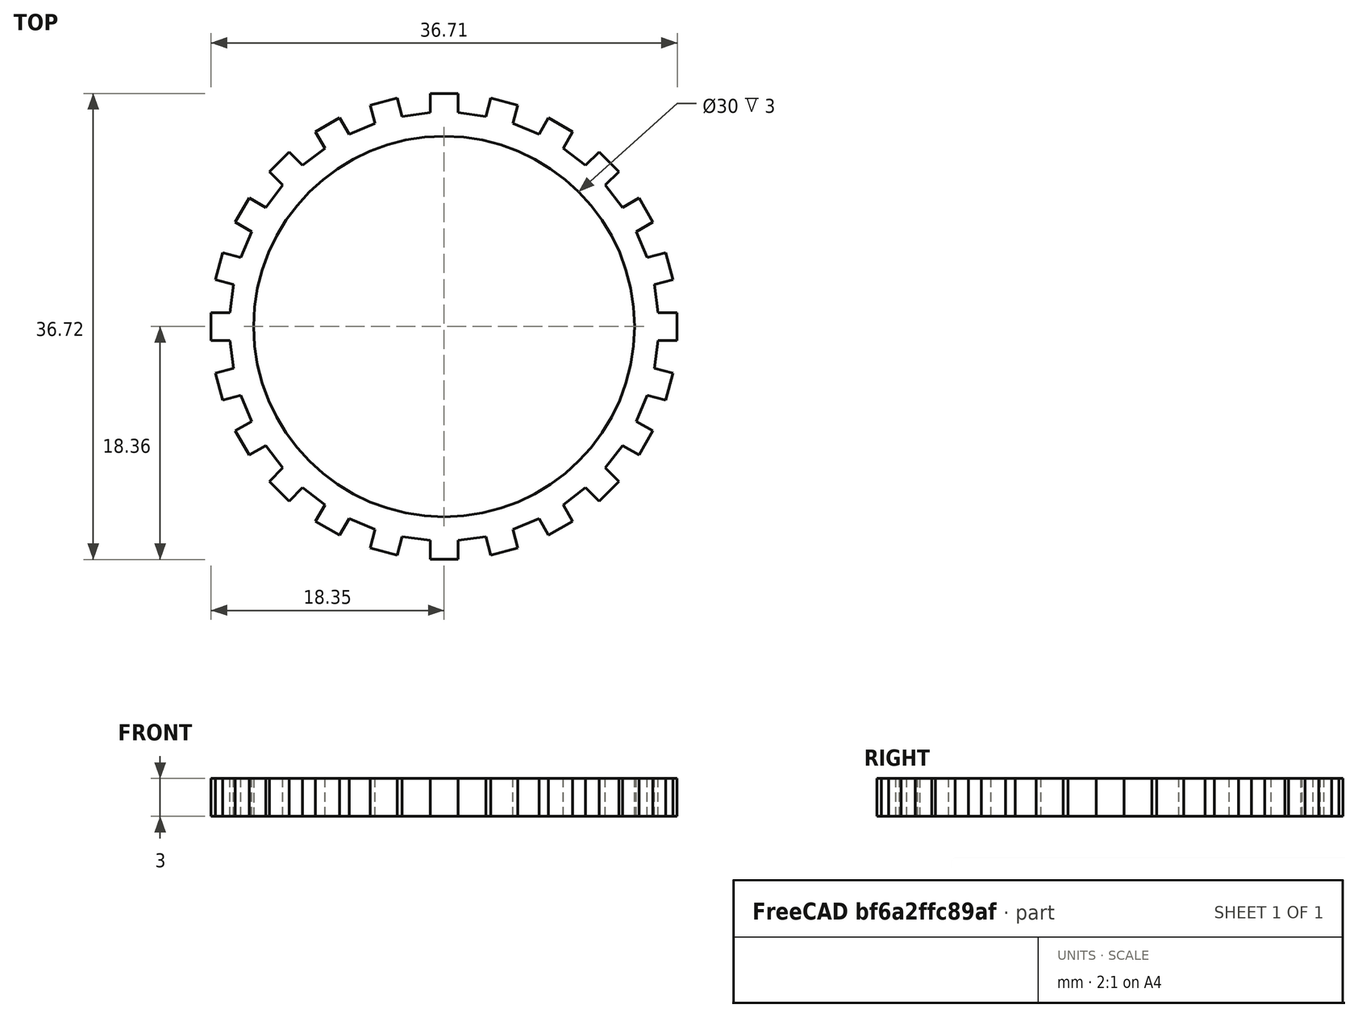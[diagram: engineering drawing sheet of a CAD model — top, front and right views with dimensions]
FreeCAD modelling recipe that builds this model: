
FCSTD DOCUMENT  (FreeCAD 0.19R24276 (Git))
Label: test_gear_1_0
License: All rights reserved
LicenseURL: http://en.wikipedia.org/wiki/All_rights_reserved
objects: Sketcher::SketchObject×1, PartDesign::Pad×1, PartDesign::Body×1
note: 4 computed .brp shape members not serialized (recipe doc carries the construction recipe); baked Part::Feature solids carry a one-line shape summary decoded from their .brp

FEATURE [Sketcher::SketchObject] Sketch
  FullyConstrained = false
  MapMode = 5
  Support = -> [XY_Plane]
  sketch-geometry (310):
    g0: Circle CenterX=0 CenterY=0 CenterZ=0 NormalX=0 NormalY=0 NormalZ=1 AngleXU=0 Radius=16.855
    g1: LineSegment StartX=0 StartY=16.855 StartZ=0 EndX=0 EndY=0 EndZ=0
    g2: LineSegment StartX=-4.3624 StartY=16.2807 StartZ=0 EndX=0 EndY=0 EndZ=0
    g3: LineSegment StartX=0 StartY=0 StartZ=0 EndX=4.3624 EndY=16.2807 EndZ=0
    g4: LineSegment StartX=0 StartY=0 StartZ=0 EndX=8.4275 EndY=14.5969 EndZ=0
    g5: LineSegment StartX=0 StartY=0 StartZ=0 EndX=11.9183 EndY=11.9183 EndZ=0
    g6: LineSegment StartX=0 StartY=0 StartZ=0 EndX=14.5969 EndY=8.4275 EndZ=0
    g7: LineSegment StartX=0 StartY=0 StartZ=0 EndX=16.2807 EndY=4.3624 EndZ=0
    g8: LineSegment StartX=0 StartY=0 StartZ=0 EndX=16.855 EndY=2.6e-15 EndZ=0
    g9: LineSegment StartX=-1.1 StartY=18.355 StartZ=0 EndX=-1.1 EndY=16.855 EndZ=0
    g10: LineSegment StartX=-1.1 StartY=16.855 StartZ=0 EndX=1.1 EndY=16.855 EndZ=0
    g11: LineSegment StartX=-1.1 StartY=18.355 StartZ=0 EndX=1.1 EndY=18.355 EndZ=0
    g12: GeomPoint X=0 Y=16.855 Z=0
    g13: LineSegment StartX=3.68811 StartY=18.0143 StartZ=0 EndX=3.29988 EndY=16.5654 EndZ=0
    g14: LineSegment StartX=3.29988 StartY=16.5654 StartZ=0 EndX=5.42491 EndY=15.996 EndZ=0
    g15: LineSegment StartX=3.68811 StartY=18.0143 StartZ=0 EndX=5.81314 EndY=17.4449 EndZ=0
    g16: LineSegment StartX=5.81314 StartY=17.4449 StartZ=0 EndX=5.42491 EndY=15.996 EndZ=0
    g17: GeomPoint X=4.3624 Y=16.2807 Z=0
    g18: LineSegment StartX=-10.1301 StartY=15.3459 StartZ=0 EndX=-9.38013 EndY=14.0469 EndZ=0
    g19: LineSegment StartX=-9.38013 StartY=14.0469 StartZ=0 EndX=-7.47487 EndY=15.1469 EndZ=0
    g20: LineSegment StartX=-10.1301 StartY=15.3459 StartZ=0 EndX=-8.22487 EndY=16.4459 EndZ=0
    g21: LineSegment StartX=-8.22487 StartY=16.4459 StartZ=0 EndX=-7.47487 EndY=15.1469 EndZ=0
    g22: GeomPoint X=-8.4275 Y=14.5969 Z=0
    g23: LineSegment StartX=0 StartY=0 StartZ=0 EndX=-8.4275 EndY=14.5969 EndZ=0
    g24: LineSegment StartX=-13.7568 StartY=12.2011 StartZ=0 EndX=-12.6961 EndY=11.1405 EndZ=0
    g25: LineSegment StartX=-12.6961 StartY=11.1405 StartZ=0 EndX=-11.1405 EndY=12.6961 EndZ=0
    g26: LineSegment StartX=-13.7568 StartY=12.2011 StartZ=0 EndX=-12.2011 EndY=13.7568 EndZ=0
    g27: LineSegment StartX=-12.2011 StartY=13.7568 StartZ=0 EndX=-11.1405 EndY=12.6961 EndZ=0
    g28: GeomPoint X=-11.9183 Y=11.9183 Z=0
    g29: LineSegment StartX=0 StartY=0 StartZ=0 EndX=-11.9183 EndY=11.9183 EndZ=0
    g30: LineSegment StartX=-5.81314 StartY=17.4449 StartZ=0 EndX=-5.42491 EndY=15.996 EndZ=0
    g31: LineSegment StartX=-5.42491 StartY=15.996 StartZ=0 EndX=-3.29988 EndY=16.5654 EndZ=0
    g32: LineSegment StartX=-5.81314 StartY=17.4449 StartZ=0 EndX=-3.68811 EndY=18.0143 EndZ=0
    g33: LineSegment StartX=-3.68811 StartY=18.0143 StartZ=0 EndX=-3.29988 EndY=16.5654 EndZ=0
    g34: GeomPoint X=-4.3624 Y=16.2807 Z=0
    g35: LineSegment StartX=8.22487 StartY=16.4459 StartZ=0 EndX=7.47487 EndY=15.1469 EndZ=0
    g36: LineSegment StartX=7.47487 StartY=15.1469 StartZ=0 EndX=9.38013 EndY=14.0469 EndZ=0
    g37: LineSegment StartX=8.22487 StartY=16.4459 StartZ=0 EndX=10.1301 EndY=15.3459 EndZ=0
    g38: LineSegment StartX=10.1301 StartY=15.3459 StartZ=0 EndX=9.38013 EndY=14.0469 EndZ=0
    g39: GeomPoint X=8.4275 Y=14.5969 Z=0
    g40: LineSegment StartX=12.2011 StartY=13.7568 StartZ=0 EndX=11.1405 EndY=12.6961 EndZ=0
    g41: LineSegment StartX=11.1405 StartY=12.6961 StartZ=0 EndX=12.6961 EndY=11.1405 EndZ=0
    g42: LineSegment StartX=12.2011 StartY=13.7568 StartZ=0 EndX=13.7568 EndY=12.2011 EndZ=0
    g43: LineSegment StartX=13.7568 StartY=12.2011 StartZ=0 EndX=12.6961 EndY=11.1405 EndZ=0
    g44: GeomPoint X=11.9183 Y=11.9183 Z=0
    g45: LineSegment StartX=15.3459 StartY=10.1301 StartZ=0 EndX=14.0469 EndY=9.38013 EndZ=0
    g46: LineSegment StartX=14.0469 StartY=9.38013 StartZ=0 EndX=15.1469 EndY=7.47487 EndZ=0
    g47: LineSegment StartX=15.3459 StartY=10.1301 StartZ=0 EndX=16.4459 EndY=8.22487 EndZ=0
    g48: LineSegment StartX=16.4459 StartY=8.22487 StartZ=0 EndX=15.1469 EndY=7.47487 EndZ=0
    g49: GeomPoint X=14.5969 Y=8.4275 Z=0
    g50: LineSegment StartX=17.4449 StartY=5.81314 StartZ=0 EndX=15.996 EndY=5.42491 EndZ=0
    g51: LineSegment StartX=15.996 StartY=5.42491 StartZ=0 EndX=16.5654 EndY=3.29988 EndZ=0
    g52: LineSegment StartX=17.4449 StartY=5.81314 StartZ=0 EndX=18.0143 EndY=3.68811 EndZ=0
    g53: LineSegment StartX=18.0143 StartY=3.68811 StartZ=0 EndX=16.5654 EndY=3.29988 EndZ=0
    g54: GeomPoint X=16.2807 Y=4.3624 Z=0
    g55: LineSegment StartX=0 StartY=0 StartZ=0 EndX=16.855 EndY=3.2e-15 EndZ=0
    g56: LineSegment StartX=18.355 StartY=1.1 StartZ=0 EndX=16.855 EndY=1.1 EndZ=0
    g57: LineSegment StartX=16.855 StartY=1.1 StartZ=0 EndX=16.855 EndY=-1.1 EndZ=0
    g58: LineSegment StartX=18.355 StartY=1.1 StartZ=0 EndX=18.355 EndY=-1.1 EndZ=0
    g59: LineSegment StartX=18.355 StartY=-1.1 StartZ=0 EndX=16.855 EndY=-1.1 EndZ=0
    g60: GeomPoint X=16.855 Y=3.2e-15 Z=0
    g61: LineSegment StartX=18.0143 StartY=-3.68811 StartZ=0 EndX=16.5654 EndY=-3.29988 EndZ=0
    g62: LineSegment StartX=16.5654 StartY=-3.29988 StartZ=0 EndX=15.996 EndY=-5.42491 EndZ=0
    g63: LineSegment StartX=18.0143 StartY=-3.68811 StartZ=0 EndX=17.4449 EndY=-5.81314 EndZ=0
    g64: LineSegment StartX=17.4449 StartY=-5.81314 StartZ=0 EndX=15.996 EndY=-5.42491 EndZ=0
    g65: GeomPoint X=16.2807 Y=-4.3624 Z=0
    g66: LineSegment StartX=0 StartY=0 StartZ=0 EndX=16.2807 EndY=-4.3624 EndZ=0
    g67: LineSegment StartX=16.4459 StartY=-8.22487 StartZ=0 EndX=15.1469 EndY=-7.47487 EndZ=0
    g68: LineSegment StartX=15.1469 StartY=-7.47487 StartZ=0 EndX=14.0469 EndY=-9.38013 EndZ=0
    g69: LineSegment StartX=16.4459 StartY=-8.22487 StartZ=0 EndX=15.3459 EndY=-10.1301 EndZ=0
    g70: LineSegment StartX=15.3459 StartY=-10.1301 StartZ=0 EndX=14.0469 EndY=-9.38013 EndZ=0
    g71: GeomPoint X=14.5969 Y=-8.4275 Z=0
    g72: LineSegment StartX=0 StartY=0 StartZ=0 EndX=14.5969 EndY=-8.4275 EndZ=0
    g73: LineSegment StartX=-16.4459 StartY=8.22487 StartZ=0 EndX=-15.1469 EndY=7.47487 EndZ=0
    g74: LineSegment StartX=-15.1469 StartY=7.47487 StartZ=0 EndX=-14.0469 EndY=9.38013 EndZ=0
    g75: LineSegment StartX=-16.4459 StartY=8.22487 StartZ=0 EndX=-15.3459 EndY=10.1301 EndZ=0
    g76: LineSegment StartX=-15.3459 StartY=10.1301 StartZ=0 EndX=-14.0469 EndY=9.38013 EndZ=0
    g77: GeomPoint X=-14.5969 Y=8.4275 Z=0
    g78: LineSegment StartX=0 StartY=0 StartZ=0 EndX=-14.5969 EndY=8.4275 EndZ=0
    g79: LineSegment StartX=-15.1469 StartY=7.47487 StartZ=0 EndX=-16.4459 EndY=8.22487 EndZ=0
    g80: LineSegment StartX=-16.4459 StartY=8.22487 StartZ=0 EndX=-15.3459 EndY=10.1301 EndZ=0
    g81: LineSegment StartX=-15.3459 StartY=10.1301 StartZ=0 EndX=-14.0469 EndY=9.38013 EndZ=0
    g82: LineSegment StartX=-12.6961 StartY=11.1405 StartZ=0 EndX=-14.0469 EndY=9.38013 EndZ=0
    g83: LineSegment StartX=-12.6961 StartY=11.1405 StartZ=0 EndX=-13.7568 EndY=12.2011 EndZ=0
    g84: LineSegment StartX=-13.7568 StartY=12.2011 StartZ=0 EndX=-12.2011 EndY=13.7568 EndZ=0
    g85: LineSegment StartX=-12.2011 StartY=13.7568 StartZ=0 EndX=-11.1405 EndY=12.6961 EndZ=0
    g86: LineSegment StartX=-11.1405 StartY=12.6961 StartZ=0 EndX=-9.38013 EndY=14.0469 EndZ=0
    g87: LineSegment StartX=-9.38013 StartY=14.0469 StartZ=0 EndX=-10.1301 EndY=15.3459 EndZ=0
    g88: LineSegment StartX=-10.1301 StartY=15.3459 StartZ=0 EndX=-8.22487 EndY=16.4459 EndZ=0
    g89: LineSegment StartX=-8.22487 StartY=16.4459 StartZ=0 EndX=-7.47487 EndY=15.1469 EndZ=0
    g90: LineSegment StartX=-7.47487 StartY=15.1469 StartZ=0 EndX=-5.42491 EndY=15.996 EndZ=0
    g91: LineSegment StartX=-5.42491 StartY=15.996 StartZ=0 EndX=-5.81314 EndY=17.4449 EndZ=0
    g92: LineSegment StartX=-5.81314 StartY=17.4449 StartZ=0 EndX=-3.68811 EndY=18.0143 EndZ=0
    g93: LineSegment StartX=-3.68811 StartY=18.0143 StartZ=0 EndX=-3.29988 EndY=16.5654 EndZ=0
    g94: LineSegment StartX=-3.29988 StartY=16.5654 StartZ=0 EndX=-1.1 EndY=16.855 EndZ=0
    g95: LineSegment StartX=-1.1 StartY=16.855 StartZ=0 EndX=-1.1 EndY=18.355 EndZ=0
    g96: LineSegment StartX=-1.1 StartY=18.355 StartZ=0 EndX=1.1 EndY=18.355 EndZ=0
    g97: LineSegment StartX=-18.0156 StartY=3.68811 StartZ=0 EndX=-16.5667 EndY=3.29988 EndZ=0
    g98: LineSegment StartX=-16.5667 StartY=3.29988 StartZ=0 EndX=-15.9973 EndY=5.42491 EndZ=0
    g99: LineSegment StartX=-18.0156 StartY=3.68811 StartZ=0 EndX=-17.4462 EndY=5.81314 EndZ=0
    g100: LineSegment StartX=-17.4462 StartY=5.81314 StartZ=0 EndX=-15.9973 EndY=5.42491 EndZ=0
    g101: GeomPoint X=-16.282 Y=4.3624 Z=0
    g102: LineSegment StartX=-0.00134425 StartY=1.8e-15 StartZ=0 EndX=-16.282 EndY=4.3624 EndZ=0
    g103: LineSegment StartX=-16.5667 StartY=3.29988 StartZ=0 EndX=-18.0156 EndY=3.68811 EndZ=0
    g104: LineSegment StartX=-18.0156 StartY=3.68811 StartZ=0 EndX=-17.4462 EndY=5.81314 EndZ=0
    g105: LineSegment StartX=-17.4462 StartY=5.81314 StartZ=0 EndX=-15.9973 EndY=5.42491 EndZ=0
    g106: LineSegment StartX=-18.3549 StartY=-1.1 StartZ=0 EndX=-16.8549 EndY=-1.1 EndZ=0
    g107: LineSegment StartX=-16.8549 StartY=-1.1 StartZ=0 EndX=-16.8549 EndY=1.1 EndZ=0
    g108: LineSegment StartX=-18.3549 StartY=-1.1 StartZ=0 EndX=-18.3549 EndY=1.1 EndZ=0
    g109: LineSegment StartX=-18.3549 StartY=1.1 StartZ=0 EndX=-16.8549 EndY=1.1 EndZ=0
    g110: GeomPoint X=-16.8549 Y=-6.7e-15 Z=0
    g111: LineSegment StartX=9.05985e-05 StartY=2.3e-15 StartZ=0 EndX=-16.8549 EndY=-6.7e-15 EndZ=0
    g112: LineSegment StartX=-18.3549 StartY=-1.1 StartZ=0 EndX=-18.3549 EndY=1.1 EndZ=0
    g113: LineSegment StartX=-18.3549 StartY=1.1 StartZ=0 EndX=-16.8549 EndY=1.1 EndZ=0
    g114: LineSegment StartX=-15.1469 StartY=7.47487 StartZ=0 EndX=-15.9973 EndY=5.42491 EndZ=0
    g115: LineSegment StartX=-16.5667 StartY=3.29988 StartZ=0 EndX=-16.8549 EndY=1.1 EndZ=0
    g116: LineSegment StartX=4.3624 StartY=16.2807 StartZ=0 EndX=0 EndY=0 EndZ=0
    g117: LineSegment StartX=1.1 StartY=18.355 StartZ=0 EndX=1.1 EndY=16.855 EndZ=0
    g118: GeomPoint X=0 Y=16.855 Z=0
    g119: LineSegment StartX=10.1301 StartY=15.3459 StartZ=0 EndX=9.38013 EndY=14.0469 EndZ=0
    g120: LineSegment StartX=9.38013 StartY=14.0469 StartZ=0 EndX=7.47487 EndY=15.1469 EndZ=0
    g121: LineSegment StartX=10.1301 StartY=15.3459 StartZ=0 EndX=8.22487 EndY=16.4459 EndZ=0
    g122: LineSegment StartX=8.22487 StartY=16.4459 StartZ=0 EndX=7.47487 EndY=15.1469 EndZ=0
    g123: GeomPoint X=8.4275 Y=14.5969 Z=0
    g124: LineSegment StartX=0 StartY=0 StartZ=0 EndX=8.4275 EndY=14.5969 EndZ=0
    g125: LineSegment StartX=13.7568 StartY=12.2011 StartZ=0 EndX=12.6961 EndY=11.1405 EndZ=0
    g126: LineSegment StartX=12.6961 StartY=11.1405 StartZ=0 EndX=11.1405 EndY=12.6961 EndZ=0
    g127: LineSegment StartX=13.7568 StartY=12.2011 StartZ=0 EndX=12.2011 EndY=13.7568 EndZ=0
    g128: LineSegment StartX=12.2011 StartY=13.7568 StartZ=0 EndX=11.1405 EndY=12.6961 EndZ=0
    g129: GeomPoint X=11.9183 Y=11.9183 Z=0
    g130: LineSegment StartX=0 StartY=0 StartZ=0 EndX=11.9183 EndY=11.9183 EndZ=0
    g131: LineSegment StartX=5.81314 StartY=17.4449 StartZ=0 EndX=5.42491 EndY=15.996 EndZ=0
    g132: LineSegment StartX=5.42491 StartY=15.996 StartZ=0 EndX=3.29988 EndY=16.5654 EndZ=0
    g133: LineSegment StartX=5.81314 StartY=17.4449 StartZ=0 EndX=3.68811 EndY=18.0143 EndZ=0
    g134: LineSegment StartX=3.68811 StartY=18.0143 StartZ=0 EndX=3.29988 EndY=16.5654 EndZ=0
    g135: GeomPoint X=4.3624 Y=16.2807 Z=0
    g136: LineSegment StartX=16.4459 StartY=8.22487 StartZ=0 EndX=15.1469 EndY=7.47487 EndZ=0
    g137: LineSegment StartX=15.1469 StartY=7.47487 StartZ=0 EndX=14.0469 EndY=9.38013 EndZ=0
    g138: LineSegment StartX=16.4459 StartY=8.22487 StartZ=0 EndX=15.3459 EndY=10.1301 EndZ=0
    g139: LineSegment StartX=15.3459 StartY=10.1301 StartZ=0 EndX=14.0469 EndY=9.38013 EndZ=0
    g140: GeomPoint X=14.5969 Y=8.4275 Z=0
    g141: LineSegment StartX=0 StartY=0 StartZ=0 EndX=14.5969 EndY=8.4275 EndZ=0
    g142: LineSegment StartX=15.1469 StartY=7.47487 StartZ=0 EndX=16.4459 EndY=8.22487 EndZ=0
    g143: LineSegment StartX=16.4459 StartY=8.22487 StartZ=0 EndX=15.3459 EndY=10.1301 EndZ=0
    g144: LineSegment StartX=15.3459 StartY=10.1301 StartZ=0 EndX=14.0469 EndY=9.38013 EndZ=0
    g145: LineSegment StartX=12.6961 StartY=11.1405 StartZ=0 EndX=14.0469 EndY=9.38013 EndZ=0
    g146: LineSegment StartX=12.6961 StartY=11.1405 StartZ=0 EndX=13.7568 EndY=12.2011 EndZ=0
    g147: LineSegment StartX=13.7568 StartY=12.2011 StartZ=0 EndX=12.2011 EndY=13.7568 EndZ=0
    g148: LineSegment StartX=12.2011 StartY=13.7568 StartZ=0 EndX=11.1405 EndY=12.6961 EndZ=0
    g149: LineSegment StartX=11.1405 StartY=12.6961 StartZ=0 EndX=9.38013 EndY=14.0469 EndZ=0
    g150: LineSegment StartX=9.38013 StartY=14.0469 StartZ=0 EndX=10.1301 EndY=15.3459 EndZ=0
    g151: LineSegment StartX=10.1301 StartY=15.3459 StartZ=0 EndX=8.22487 EndY=16.4459 EndZ=0
    g152: LineSegment StartX=8.22487 StartY=16.4459 StartZ=0 EndX=7.47487 EndY=15.1469 EndZ=0
    g153: LineSegment StartX=7.47487 StartY=15.1469 StartZ=0 EndX=5.42491 EndY=15.996 EndZ=0
    g154: LineSegment StartX=5.42491 StartY=15.996 StartZ=0 EndX=5.81314 EndY=17.4449 EndZ=0
    g155: LineSegment StartX=5.81314 StartY=17.4449 StartZ=0 EndX=3.68811 EndY=18.0143 EndZ=0
    g156: LineSegment StartX=3.68811 StartY=18.0143 StartZ=0 EndX=3.29988 EndY=16.5654 EndZ=0
    g157: LineSegment StartX=3.29988 StartY=16.5654 StartZ=0 EndX=1.1 EndY=16.855 EndZ=0
    g158: LineSegment StartX=18.0156 StartY=3.68811 StartZ=0 EndX=16.5667 EndY=3.29988 EndZ=0
    g159: LineSegment StartX=16.5667 StartY=3.29988 StartZ=0 EndX=15.9973 EndY=5.42491 EndZ=0
    g160: LineSegment StartX=18.0156 StartY=3.68811 StartZ=0 EndX=17.4462 EndY=5.81314 EndZ=0
    g161: LineSegment StartX=17.4462 StartY=5.81314 StartZ=0 EndX=15.9973 EndY=5.42491 EndZ=0
    g162: GeomPoint X=16.282 Y=4.3624 Z=0
    g163: LineSegment StartX=0.00134425 StartY=-1.2e-15 StartZ=0 EndX=16.282 EndY=4.3624 EndZ=0
    g164: LineSegment StartX=17.4462 StartY=5.81314 StartZ=0 EndX=15.9973 EndY=5.42491 EndZ=0
    g165: LineSegment StartX=18.3549 StartY=-1.1 StartZ=0 EndX=16.8549 EndY=-1.1 EndZ=0
    g166: LineSegment StartX=16.8549 StartY=-1.1 StartZ=0 EndX=16.8549 EndY=1.1 EndZ=0
    g167: LineSegment StartX=18.3549 StartY=-1.1 StartZ=0 EndX=18.3549 EndY=1.1 EndZ=0
    g168: LineSegment StartX=18.3549 StartY=1.1 StartZ=0 EndX=16.8549 EndY=1.1 EndZ=0
    g169: GeomPoint X=16.8549 Y=-7.1e-15 Z=0
    g170: LineSegment StartX=-9.05985e-05 StartY=1.7e-15 StartZ=0 EndX=16.8549 EndY=-7.1e-15 EndZ=0
    g171: LineSegment StartX=18.3549 StartY=1.1 StartZ=0 EndX=16.8549 EndY=1.1 EndZ=0
    g172: LineSegment StartX=15.1469 StartY=7.47487 StartZ=0 EndX=15.9973 EndY=5.42491 EndZ=0
    g173: LineSegment StartX=16.5667 StartY=3.29988 StartZ=0 EndX=16.8549 EndY=1.1 EndZ=0
    g174: LineSegment StartX=1.1 StartY=16.855 StartZ=0 EndX=1.1 EndY=18.355 EndZ=0
    g175: LineSegment StartX=-1.1 StartY=-18.355 StartZ=0 EndX=-1.1 EndY=-16.855 EndZ=0
    g176: LineSegment StartX=-1.1 StartY=-16.855 StartZ=0 EndX=1.1 EndY=-16.855 EndZ=0
    g177: LineSegment StartX=-1.1 StartY=-18.355 StartZ=0 EndX=1.1 EndY=-18.355 EndZ=0
    g178: GeomPoint X=1.08e-14 Y=-16.855 Z=0
    g179: LineSegment StartX=3.68811 StartY=-18.0143 StartZ=0 EndX=3.29988 EndY=-16.5654 EndZ=0
    g180: LineSegment StartX=3.29988 StartY=-16.5654 StartZ=0 EndX=5.42491 EndY=-15.996 EndZ=0
    g181: LineSegment StartX=3.68811 StartY=-18.0143 StartZ=0 EndX=5.81314 EndY=-17.4449 EndZ=0
    g182: LineSegment StartX=5.81314 StartY=-17.4449 StartZ=0 EndX=5.42491 EndY=-15.996 EndZ=0
    g183: GeomPoint X=4.3624 Y=-16.2807 Z=0
    g184: LineSegment StartX=-10.1301 StartY=-15.3459 StartZ=0 EndX=-9.38013 EndY=-14.0469 EndZ=0
    g185: LineSegment StartX=-9.38013 StartY=-14.0469 StartZ=0 EndX=-7.47487 EndY=-15.1469 EndZ=0
    g186: LineSegment StartX=-10.1301 StartY=-15.3459 StartZ=0 EndX=-8.22487 EndY=-16.4459 EndZ=0
    g187: LineSegment StartX=-8.22487 StartY=-16.4459 StartZ=0 EndX=-7.47487 EndY=-15.1469 EndZ=0
    g188: GeomPoint X=-8.4275 Y=-14.5969 Z=0
    g189: LineSegment StartX=-13.7568 StartY=-12.2011 StartZ=0 EndX=-12.6961 EndY=-11.1405 EndZ=0
    g190: LineSegment StartX=-12.6961 StartY=-11.1405 StartZ=0 EndX=-11.1405 EndY=-12.6961 EndZ=0
    g191: LineSegment StartX=-13.7568 StartY=-12.2011 StartZ=0 EndX=-12.2011 EndY=-13.7568 EndZ=0
    g192: LineSegment StartX=-12.2011 StartY=-13.7568 StartZ=0 EndX=-11.1405 EndY=-12.6961 EndZ=0
    g193: GeomPoint X=-11.9183 Y=-11.9183 Z=0
    g194: LineSegment StartX=-5.81314 StartY=-17.4449 StartZ=0 EndX=-5.42491 EndY=-15.996 EndZ=0
    g195: LineSegment StartX=-5.42491 StartY=-15.996 StartZ=0 EndX=-3.29988 EndY=-16.5654 EndZ=0
    g196: LineSegment StartX=-5.81314 StartY=-17.4449 StartZ=0 EndX=-3.68811 EndY=-18.0143 EndZ=0
    g197: LineSegment StartX=-3.68811 StartY=-18.0143 StartZ=0 EndX=-3.29988 EndY=-16.5654 EndZ=0
    g198: GeomPoint X=-4.3624 Y=-16.2807 Z=0
    g199: LineSegment StartX=8.22487 StartY=-16.4459 StartZ=0 EndX=7.47487 EndY=-15.1469 EndZ=0
    g200: LineSegment StartX=7.47487 StartY=-15.1469 StartZ=0 EndX=9.38013 EndY=-14.0469 EndZ=0
    g201: LineSegment StartX=8.22487 StartY=-16.4459 StartZ=0 EndX=10.1301 EndY=-15.3459 EndZ=0
    g202: LineSegment StartX=10.1301 StartY=-15.3459 StartZ=0 EndX=9.38013 EndY=-14.0469 EndZ=0
    g203: GeomPoint X=8.4275 Y=-14.5969 Z=0
    g204: LineSegment StartX=12.2011 StartY=-13.7568 StartZ=0 EndX=11.1405 EndY=-12.6961 EndZ=0
    g205: LineSegment StartX=11.1405 StartY=-12.6961 StartZ=0 EndX=12.6961 EndY=-11.1405 EndZ=0
    g206: LineSegment StartX=12.2011 StartY=-13.7568 StartZ=0 EndX=13.7568 EndY=-12.2011 EndZ=0
    g207: LineSegment StartX=13.7568 StartY=-12.2011 StartZ=0 EndX=12.6961 EndY=-11.1405 EndZ=0
    g208: GeomPoint X=11.9183 Y=-11.9183 Z=0
    g209: LineSegment StartX=15.3459 StartY=-10.1301 StartZ=0 EndX=14.0469 EndY=-9.38013 EndZ=0
    g210: LineSegment StartX=14.0469 StartY=-9.38013 StartZ=0 EndX=15.1469 EndY=-7.47487 EndZ=0
    g211: LineSegment StartX=15.3459 StartY=-10.1301 StartZ=0 EndX=16.4459 EndY=-8.22487 EndZ=0
    g212: LineSegment StartX=16.4459 StartY=-8.22487 StartZ=0 EndX=15.1469 EndY=-7.47487 EndZ=0
    g213: GeomPoint X=14.5969 Y=-8.4275 Z=0
    g214: LineSegment StartX=17.4449 StartY=-5.81314 StartZ=0 EndX=15.996 EndY=-5.42491 EndZ=0
    g215: LineSegment StartX=15.996 StartY=-5.42491 StartZ=0 EndX=16.5654 EndY=-3.29988 EndZ=0
    g216: LineSegment StartX=17.4449 StartY=-5.81314 StartZ=0 EndX=18.0143 EndY=-3.68811 EndZ=0
    g217: LineSegment StartX=18.0143 StartY=-3.68811 StartZ=0 EndX=16.5654 EndY=-3.29988 EndZ=0
    g218: GeomPoint X=16.2807 Y=-4.3624 Z=0
    g219: LineSegment StartX=18.355 StartY=-1.1 StartZ=0 EndX=16.855 EndY=-1.1 EndZ=0
    g220: LineSegment StartX=-16.4459 StartY=-8.22487 StartZ=0 EndX=-15.1469 EndY=-7.47487 EndZ=0
    g221: LineSegment StartX=-15.1469 StartY=-7.47487 StartZ=0 EndX=-14.0469 EndY=-9.38013 EndZ=0
    g222: LineSegment StartX=-16.4459 StartY=-8.22487 StartZ=0 EndX=-15.3459 EndY=-10.1301 EndZ=0
    g223: LineSegment StartX=-15.3459 StartY=-10.1301 StartZ=0 EndX=-14.0469 EndY=-9.38013 EndZ=0
    g224: GeomPoint X=-14.5969 Y=-8.4275 Z=0
    g225: LineSegment StartX=-15.1469 StartY=-7.47487 StartZ=0 EndX=-16.4459 EndY=-8.22487 EndZ=0
    g226: LineSegment StartX=-16.4459 StartY=-8.22487 StartZ=0 EndX=-15.3459 EndY=-10.1301 EndZ=0
    g227: LineSegment StartX=-15.3459 StartY=-10.1301 StartZ=0 EndX=-14.0469 EndY=-9.38013 EndZ=0
    g228: LineSegment StartX=-12.6961 StartY=-11.1405 StartZ=0 EndX=-14.0469 EndY=-9.38013 EndZ=0
    g229: LineSegment StartX=-12.6961 StartY=-11.1405 StartZ=0 EndX=-13.7568 EndY=-12.2011 EndZ=0
    g230: LineSegment StartX=-13.7568 StartY=-12.2011 StartZ=0 EndX=-12.2011 EndY=-13.7568 EndZ=0
    g231: LineSegment StartX=-12.2011 StartY=-13.7568 StartZ=0 EndX=-11.1405 EndY=-12.6961 EndZ=0
    g232: LineSegment StartX=-11.1405 StartY=-12.6961 StartZ=0 EndX=-9.38013 EndY=-14.0469 EndZ=0
    g233: LineSegment StartX=-9.38013 StartY=-14.0469 StartZ=0 EndX=-10.1301 EndY=-15.3459 EndZ=0
    g234: LineSegment StartX=-10.1301 StartY=-15.3459 StartZ=0 EndX=-8.22487 EndY=-16.4459 EndZ=0
    g235: LineSegment StartX=-8.22487 StartY=-16.4459 StartZ=0 EndX=-7.47487 EndY=-15.1469 EndZ=0
    g236: LineSegment StartX=-7.47487 StartY=-15.1469 StartZ=0 EndX=-5.42491 EndY=-15.996 EndZ=0
    g237: LineSegment StartX=-5.42491 StartY=-15.996 StartZ=0 EndX=-5.81314 EndY=-17.4449 EndZ=0
    g238: LineSegment StartX=-5.81314 StartY=-17.4449 StartZ=0 EndX=-3.68811 EndY=-18.0143 EndZ=0
    g239: LineSegment StartX=-3.68811 StartY=-18.0143 StartZ=0 EndX=-3.29988 EndY=-16.5654 EndZ=0
    g240: LineSegment StartX=-3.29988 StartY=-16.5654 StartZ=0 EndX=-1.1 EndY=-16.855 EndZ=0
    g241: LineSegment StartX=-1.1 StartY=-16.855 StartZ=0 EndX=-1.1 EndY=-18.355 EndZ=0
    g242: LineSegment StartX=-1.1 StartY=-18.355 StartZ=0 EndX=1.1 EndY=-18.355 EndZ=0
    g243: LineSegment StartX=-18.0156 StartY=-3.68811 StartZ=0 EndX=-16.5667 EndY=-3.29988 EndZ=0
    g244: LineSegment StartX=-16.5667 StartY=-3.29988 StartZ=0 EndX=-15.9973 EndY=-5.42491 EndZ=0
    g245: LineSegment StartX=-18.0156 StartY=-3.68811 StartZ=0 EndX=-17.4462 EndY=-5.81314 EndZ=0
    g246: LineSegment StartX=-17.4462 StartY=-5.81314 StartZ=0 EndX=-15.9973 EndY=-5.42491 EndZ=0
    g247: GeomPoint X=-16.282 Y=-4.3624 Z=0
    g248: LineSegment StartX=-16.5667 StartY=-3.29988 StartZ=0 EndX=-18.0156 EndY=-3.68811 EndZ=0
    g249: LineSegment StartX=-18.0156 StartY=-3.68811 StartZ=0 EndX=-17.4462 EndY=-5.81314 EndZ=0
    g250: LineSegment StartX=-17.4462 StartY=-5.81314 StartZ=0 EndX=-15.9973 EndY=-5.42491 EndZ=0
    g251: LineSegment StartX=-18.3549 StartY=-1.1 StartZ=0 EndX=-16.8549 EndY=-1.1 EndZ=0
    g252: LineSegment StartX=-18.3549 StartY=-1.1 StartZ=0 EndX=-16.8549 EndY=-1.1 EndZ=0
    g253: LineSegment StartX=-15.1469 StartY=-7.47487 StartZ=0 EndX=-15.9973 EndY=-5.42491 EndZ=0
    g254: LineSegment StartX=-16.5667 StartY=-3.29988 StartZ=0 EndX=-16.8549 EndY=-1.1 EndZ=0
    g255: LineSegment StartX=1.1 StartY=-18.355 StartZ=0 EndX=1.1 EndY=-16.855 EndZ=0
    g256: GeomPoint X=1.08e-14 Y=-16.855 Z=0
    g257: LineSegment StartX=10.1301 StartY=-15.3459 StartZ=0 EndX=9.38013 EndY=-14.0469 EndZ=0
    g258: LineSegment StartX=9.38013 StartY=-14.0469 StartZ=0 EndX=7.47487 EndY=-15.1469 EndZ=0
    g259: LineSegment StartX=10.1301 StartY=-15.3459 StartZ=0 EndX=8.22487 EndY=-16.4459 EndZ=0
    g260: LineSegment StartX=8.22487 StartY=-16.4459 StartZ=0 EndX=7.47487 EndY=-15.1469 EndZ=0
    g261: GeomPoint X=8.4275 Y=-14.5969 Z=0
    g262: LineSegment StartX=13.7568 StartY=-12.2011 StartZ=0 EndX=12.6961 EndY=-11.1405 EndZ=0
    g263: LineSegment StartX=12.6961 StartY=-11.1405 StartZ=0 EndX=11.1405 EndY=-12.6961 EndZ=0
    g264: LineSegment StartX=13.7568 StartY=-12.2011 StartZ=0 EndX=12.2011 EndY=-13.7568 EndZ=0
    g265: LineSegment StartX=12.2011 StartY=-13.7568 StartZ=0 EndX=11.1405 EndY=-12.6961 EndZ=0
    g266: GeomPoint X=11.9183 Y=-11.9183 Z=0
    g267: LineSegment StartX=5.81314 StartY=-17.4449 StartZ=0 EndX=5.42491 EndY=-15.996 EndZ=0
    g268: LineSegment StartX=5.42491 StartY=-15.996 StartZ=0 EndX=3.29988 EndY=-16.5654 EndZ=0
    g269: LineSegment StartX=5.81314 StartY=-17.4449 StartZ=0 EndX=3.68811 EndY=-18.0143 EndZ=0
    g270: LineSegment StartX=3.68811 StartY=-18.0143 StartZ=0 EndX=3.29988 EndY=-16.5654 EndZ=0
    g271: GeomPoint X=4.3624 Y=-16.2807 Z=0
    g272: LineSegment StartX=16.4459 StartY=-8.22487 StartZ=0 EndX=15.1469 EndY=-7.47487 EndZ=0
    g273: LineSegment StartX=15.1469 StartY=-7.47487 StartZ=0 EndX=14.0469 EndY=-9.38013 EndZ=0
    g274: LineSegment StartX=16.4459 StartY=-8.22487 StartZ=0 EndX=15.3459 EndY=-10.1301 EndZ=0
    g275: LineSegment StartX=15.3459 StartY=-10.1301 StartZ=0 EndX=14.0469 EndY=-9.38013 EndZ=0
    g276: GeomPoint X=14.5969 Y=-8.4275 Z=0
    g277: LineSegment StartX=15.1469 StartY=-7.47487 StartZ=0 EndX=16.4459 EndY=-8.22487 EndZ=0
    g278: LineSegment StartX=16.4459 StartY=-8.22487 StartZ=0 EndX=15.3459 EndY=-10.1301 EndZ=0
    g279: LineSegment StartX=15.3459 StartY=-10.1301 StartZ=0 EndX=14.0469 EndY=-9.38013 EndZ=0
    g280: LineSegment StartX=12.6961 StartY=-11.1405 StartZ=0 EndX=14.0469 EndY=-9.38013 EndZ=0
    g281: LineSegment StartX=12.6961 StartY=-11.1405 StartZ=0 EndX=13.7568 EndY=-12.2011 EndZ=0
    g282: LineSegment StartX=13.7568 StartY=-12.2011 StartZ=0 EndX=12.2011 EndY=-13.7568 EndZ=0
    g283: LineSegment StartX=12.2011 StartY=-13.7568 StartZ=0 EndX=11.1405 EndY=-12.6961 EndZ=0
    g284: LineSegment StartX=11.1405 StartY=-12.6961 StartZ=0 EndX=9.38013 EndY=-14.0469 EndZ=0
    g285: LineSegment StartX=9.38013 StartY=-14.0469 StartZ=0 EndX=10.1301 EndY=-15.3459 EndZ=0
    g286: LineSegment StartX=10.1301 StartY=-15.3459 StartZ=0 EndX=8.22487 EndY=-16.4459 EndZ=0
    g287: LineSegment StartX=8.22487 StartY=-16.4459 StartZ=0 EndX=7.47487 EndY=-15.1469 EndZ=0
    g288: LineSegment StartX=7.47487 StartY=-15.1469 StartZ=0 EndX=5.42491 EndY=-15.996 EndZ=0
    g289: LineSegment StartX=5.42491 StartY=-15.996 StartZ=0 EndX=5.81314 EndY=-17.4449 EndZ=0
    g290: LineSegment StartX=5.81314 StartY=-17.4449 StartZ=0 EndX=3.68811 EndY=-18.0143 EndZ=0
    g291: LineSegment StartX=3.68811 StartY=-18.0143 StartZ=0 EndX=3.29988 EndY=-16.5654 EndZ=0
    g292: LineSegment StartX=3.29988 StartY=-16.5654 StartZ=0 EndX=1.1 EndY=-16.855 EndZ=0
    g293: LineSegment StartX=18.0156 StartY=-3.68811 StartZ=0 EndX=16.5667 EndY=-3.29988 EndZ=0
    g294: LineSegment StartX=16.5667 StartY=-3.29988 StartZ=0 EndX=15.9973 EndY=-5.42491 EndZ=0
    g295: LineSegment StartX=18.0156 StartY=-3.68811 StartZ=0 EndX=17.4462 EndY=-5.81314 EndZ=0
    g296: LineSegment StartX=17.4462 StartY=-5.81314 StartZ=0 EndX=15.9973 EndY=-5.42491 EndZ=0
    g297: GeomPoint X=16.282 Y=-4.3624 Z=0
    g298: LineSegment StartX=16.5667 StartY=-3.29988 StartZ=0 EndX=18.0156 EndY=-3.68811 EndZ=0
    g299: LineSegment StartX=18.0156 StartY=-3.68811 StartZ=0 EndX=17.4462 EndY=-5.81314 EndZ=0
    g300: LineSegment StartX=17.4462 StartY=-5.81314 StartZ=0 EndX=15.9973 EndY=-5.42491 EndZ=0
    g301: LineSegment StartX=18.3549 StartY=-1.1 StartZ=0 EndX=16.8549 EndY=-1.1 EndZ=0
    g302: LineSegment StartX=15.1469 StartY=-7.47487 StartZ=0 EndX=15.9973 EndY=-5.42491 EndZ=0
    g303: LineSegment StartX=16.5667 StartY=-3.29988 StartZ=0 EndX=16.8549 EndY=-1.1 EndZ=0
    g304: LineSegment StartX=1.1 StartY=-16.855 StartZ=0 EndX=1.1 EndY=-18.355 EndZ=0
    g305: Circle CenterX=0 CenterY=0 CenterZ=0 NormalX=0 NormalY=0 NormalZ=1 AngleXU=0 Radius=15
    g306: LineSegment StartX=18.0156 StartY=3.68811 StartZ=0 EndX=16.5667 EndY=3.29988 EndZ=0
    g307: LineSegment StartX=17.4462 StartY=5.81314 StartZ=0 EndX=18.0156 EndY=3.68811 EndZ=0
    g308: LineSegment StartX=18.3549 StartY=1.1 StartZ=0 EndX=18.355 EndY=-1.1 EndZ=0
    g309: LineSegment StartX=18.355 StartY=-1.1 StartZ=0 EndX=16.8549 EndY=-1.1 EndZ=0
  constraints (689):
    c: Diameter(g0) = 33.71
    c: Vertical(g1)
    c: Coincident(g0,g-1)
    c: Coincident(g1,g0)
    c: Coincident(g2,g0)
    c: Angle(g1,g2) = 0.261799
    c: Coincident(g3,g0)
    c: Angle(g3,g1) = 0.261799
    c: PointOnObject(g3,g0)
    c: PointOnObject(g1,g0)
    c: PointOnObject(g2,g0)
    c: Coincident(g4,g0)
    c: Angle(g4,g3) = 0.261799
    c: PointOnObject(g4,g0)
    c: Coincident(g5,g0)
    c: Angle(g5,g4) = 0.261799
    c: Coincident(g6,g0)
    c: Angle(g6,g5) = 0.261799
    c: Coincident(g7,g0)
    c: Angle(g7,g6) = 0.261799
    c: Coincident(g8,g0)
    c: Angle(g8,g7) = 0.261799
    c: PointOnObject(g5,g0)
    c: PointOnObject(g7,g0)
    c: PointOnObject(g6,g0)
    c: PointOnObject(g8,g0)
    c: Coincident(g10,g9)
    c: Coincident(g11,g9)
    c: Parallel(g10,g11)
    c: Perpendicular(g10,g9)
    c: Distance(g9,g11) = 2.2
    c: Distance(g11,g10) = 1.5
    c: PointOnObject(g12,g10)
    c: Distance(g9,g12) = 1.1
    c: Coincident(g12,g1)
    c: Perpendicular(g1,g10)
    c: Coincident(g14,g13)
    c: Coincident(g15,g13)
    c: Coincident(g16,g15)
    c: Coincident(g16,g14)
    c: Parallel(g14,g15)
    c: Parallel(g13,g16)
    c: Perpendicular(g14,g13)
    c: Distance(g13,g15) = 2.2
    c: Distance(g15,g14) = 1.5
    c: PointOnObject(g17,g14)
    c: Distance(g13,g17) = 1.1
    c: Coincident(g17,g3)
    c: Perpendicular(g3,g14)
    c: Coincident(g19,g18)
    c: Coincident(g20,g18)
    c: Coincident(g21,g20)
    c: Coincident(g21,g19)
    c: Parallel(g19,g20)
    c: Parallel(g18,g21)
    c: Perpendicular(g19,g18)
    c: Distance(g18,g20) = 2.2
    c: Distance(g20,g19) = 1.5
    c: PointOnObject(g22,g19)
    c: Distance(g18,g22) = 1.1
    c: Perpendicular(g23,g19)
    c: Coincident(g23,g0)
    c: Angle(g23,g2) = -0.261799
    c: PointOnObject(g23,g0)
    c: Coincident(g22,g23)
    c: Coincident(g25,g24)
    c: Coincident(g26,g24)
    c: Coincident(g27,g26)
    c: Coincident(g27,g25)
    c: Parallel(g25,g26)
    c: Parallel(g24,g27)
    c: Perpendicular(g25,g24)
    c: Distance(g24,g26) = 2.2
    c: Distance(g26,g25) = 1.5
    c: PointOnObject(g28,g25)
    c: Distance(g24,g28) = 1.1
    c: Perpendicular(g29,g25)
    c: Coincident(g28,g29)
    c: Equal(g29,g23)
    c: Coincident(g29,g0)
    c: Angle(g23,g29) = 0.261799
    c: Coincident(g31,g30)
    c: Coincident(g32,g30)
    c: Coincident(g33,g32)
    c: Coincident(g33,g31)
    c: Parallel(g31,g32)
    c: Parallel(g30,g33)
    c: Perpendicular(g31,g30)
    c: Distance(g30,g32) = 2.2
    c: Distance(g32,g31) = 1.5
    c: PointOnObject(g34,g31)
    c: Distance(g30,g34) = 1.1
    c: Coincident(g34,g2)
    c: Perpendicular(g2,g31)
    c: Coincident(g36,g35)
    c: Coincident(g37,g35)
    c: Coincident(g38,g37)
    c: Coincident(g38,g36)
    c: Parallel(g36,g37)
    c: Parallel(g35,g38)
    c: Perpendicular(g36,g35)
    c: Distance(g35,g37) = 2.2
    c: Distance(g37,g36) = 1.5
    c: PointOnObject(g39,g36)
    c: Distance(g35,g39) = 1.1
    c: Coincident(g39,g4)
    c: Perpendicular(g4,g36)
    c: Coincident(g41,g40)
    c: Coincident(g42,g40)
    c: Coincident(g43,g42)
    c: Coincident(g43,g41)
    c: Parallel(g41,g42)
    c: Parallel(g40,g43)
    c: Perpendicular(g41,g40)
    c: Distance(g40,g42) = 2.2
    c: Distance(g42,g41) = 1.5
    c: PointOnObject(g44,g41)
    c: Distance(g40,g44) = 1.1
    c: Coincident(g5,g44)
    c: Perpendicular(g5,g41)
    c: Coincident(g46,g45)
    c: Coincident(g47,g45)
    c: Coincident(g48,g47)
    c: Coincident(g48,g46)
    c: Parallel(g46,g47)
    c: Parallel(g45,g48)
    c: Perpendicular(g46,g45)
    c: Distance(g45,g47) = 2.2
    c: Distance(g47,g46) = 1.5
    c: PointOnObject(g49,g46)
    c: Distance(g45,g49) = 1.1
    c: Coincident(g49,g6)
    c: Perpendicular(g46,g6)
    c: Coincident(g51,g50)
    c: Coincident(g52,g50)
    c: Coincident(g53,g52)
    c: Coincident(g53,g51)
    c: Parallel(g51,g52)
    c: Parallel(g50,g53)
    c: Perpendicular(g51,g50)
    c: Distance(g50,g52) = 2.2
    c: Distance(g52,g51) = 1.5
    c: PointOnObject(g54,g51)
    c: Distance(g50,g54) = 1.1
    c: Coincident(g54,g7)
    c: Perpendicular(g7,g51)
    c: Coincident(g57,g56)
    c: Coincident(g58,g56)
    c: Coincident(g59,g58)
    c: Coincident(g59,g57)
    c: Parallel(g57,g58)
    c: Parallel(g56,g59)
    c: Perpendicular(g57,g56)
    c: Distance(g56,g58) = 2.2
    c: Distance(g58,g57) = 1.5
    c: PointOnObject(g60,g57)
    c: Distance(g56,g60) = 1.1
    c: Coincident(g60,g55)
    c: Perpendicular(g55,g57)
    c: Equal(g55,g7)
    c: Coincident(g55,g0)
    c: Angle(g55,g7) = 0.261799
    c: Coincident(g62,g61)
    c: Coincident(g63,g61)
    c: Coincident(g64,g63)
    c: Coincident(g64,g62)
    c: Parallel(g62,g63)
    c: Parallel(g61,g64)
    c: Perpendicular(g62,g61)
    c: Distance(g61,g63) = 2.2
    c: Distance(g63,g62) = 1.5
    c: PointOnObject(g65,g62)
    c: Distance(g61,g65) = 1.1
    c: Equal(g7,g66)
    c: Coincident(g66,g65)
    c: Perpendicular(g62,g66)
    c: Coincident(g66,g0)
    c: Angle(g66,g8) = 0.261799
    c: Coincident(g68,g67)
    c: Coincident(g69,g67)
    c: Coincident(g70,g69)
    c: Coincident(g70,g68)
    c: Parallel(g68,g69)
    c: Parallel(g67,g70)
    c: Perpendicular(g68,g67)
    c: Distance(g67,g69) = 2.2
    c: Distance(g69,g68) = 1.5
    c: PointOnObject(g71,g68)
    c: Distance(g67,g71) = 1.1
    c: Perpendicular(g72,g68)
    c: Coincident(g71,g72)
    c: Equal(g72,g66)
    c: Coincident(g72,g0)
    c: Angle(g72,g66) = 0.261799
    c: Coincident(g74,g73)
    c: Coincident(g75,g73)
    c: Coincident(g76,g75)
    c: Coincident(g76,g74)
    c: Parallel(g74,g75)
    c: Parallel(g73,g76)
    c: Perpendicular(g74,g73)
    c: Distance(g73,g75) = 2.2
    c: Distance(g75,g74) = 1.5
    c: PointOnObject(g77,g74)
    c: Distance(g73,g77) = 1.1
    c: Perpendicular(g78,g74)
    c: Coincident(g77,g78)
    c: Equal(g29,g78)
    c: Coincident(g78,g0)
    c: Angle(g29,g78) = 0.261799
    c: Coincident(g79,g73)
    c: Coincident(g79,g73)
    c: Coincident(g80,g79)
    c: Coincident(g80,g75)
    c: Coincident(g81,g80)
    c: Coincident(g81,g74)
    c: Coincident(g82,g24)
    c: Coincident(g82,g81)
    c: Coincident(g83,g82)
    c: Coincident(g83,g24)
    c: Coincident(g84,g83)
    c: Coincident(g84,g26)
    c: Coincident(g85,g84)
    c: Coincident(g85,g25)
    c: Coincident(g86,g85)
    c: Coincident(g86,g18)
    c: Coincident(g87,g86)
    c: Coincident(g87,g18)
    c: Coincident(g88,g87)
    c: Coincident(g88,g20)
    c: Coincident(g89,g88)
    c: Coincident(g89,g19)
    c: Coincident(g90,g89)
    c: Coincident(g90,g30)
    c: Coincident(g91,g90)
    c: Coincident(g91,g30)
    c: Coincident(g92,g91)
    c: Coincident(g92,g32)
    c: Coincident(g93,g92)
    c: Coincident(g93,g31)
    c: Coincident(g94,g93)
    c: Coincident(g94,g9)
    c: Coincident(g95,g94)
    c: PointOnObject(g95,g11)
    c: Vertical(g95)
    c: Coincident(g96,g95)
    c: Coincident(g96,g11)
    c: Coincident(g98,g97)
    c: Coincident(g99,g97)
    c: Coincident(g100,g99)
    c: Coincident(g100,g98)
    c: Parallel(g98,g99)
    c: Parallel(g97,g100)
    c: Perpendicular(g98,g97)
    c: Distance(g97,g99) = 2.2
    c: Distance(g99,g98) = 1.5
    c: PointOnObject(g101,g98)
    c: Distance(g97,g101) = 1.1
    c: Perpendicular(g102,g98)
    c: Coincident(g101,g102)
    c: Coincident(g103,g97)
    c: Coincident(g103,g97)
    c: Coincident(g104,g103)
    c: Coincident(g104,g99)
    c: Coincident(g105,g104)
    c: Coincident(g105,g98)
    c: Equal(g102,g78)
    c: Angle(g78,g102) = 0.261799
    c: Coincident(g107,g106)
    c: Coincident(g108,g106)
    c: Coincident(g109,g108)
    c: Coincident(g109,g107)
    c: Parallel(g107,g108)
    c: Parallel(g106,g109)
    c: Perpendicular(g107,g106)
    c: Distance(g106,g108) = 2.2
    c: Distance(g108,g107) = 1.5
    c: PointOnObject(g110,g107)
    c: Distance(g106,g110) = 1.1
    c: Perpendicular(g111,g107)
    c: Coincident(g110,g111)
    c: Coincident(g112,g108)
    c: Coincident(g113,g112)
    c: Coincident(g113,g107)
    c: Equal(g111,g102)
    c: Angle(g102,g111) = 0.261799
    c: Coincident(g114,g79)
    c: Coincident(g114,g105)
    c: Coincident(g115,g103)
    c: Coincident(g115,g113)
    c: Distance(g117,g118) = 1.1
    c: Coincident(g120,g119)
    c: Coincident(g121,g119)
    c: Coincident(g122,g121)
    c: Coincident(g122,g120)
    c: Parallel(g120,g121)
    c: Parallel(g119,g122)
    c: Perpendicular(g120,g119)
    c: Distance(g119,g121) = 2.2
    c: Distance(g121,g120) = 1.5
    c: PointOnObject(g123,g120)
    c: Distance(g119,g123) = 1.1
    c: Perpendicular(g124,g120)
    c: Angle(g124,g116) = 0.261799
    c: Coincident(g123,g124)
    c: Coincident(g126,g125)
    c: Coincident(g127,g125)
    c: Coincident(g128,g127)
    c: Coincident(g128,g126)
    c: Parallel(g126,g127)
    c: Parallel(g125,g128)
    c: Perpendicular(g126,g125)
    c: Distance(g125,g127) = 2.2
    c: Distance(g127,g126) = 1.5
    c: PointOnObject(g129,g126)
    c: Distance(g125,g129) = 1.1
    c: Perpendicular(g130,g126)
    c: Coincident(g129,g130)
    c: Equal(g130,g124)
    c: Angle(g124,g130) = -0.261799
    c: Coincident(g132,g131)
    c: Coincident(g133,g131)
    c: Coincident(g134,g133)
    c: Coincident(g134,g132)
    c: Parallel(g132,g133)
    c: Parallel(g131,g134)
    c: Perpendicular(g132,g131)
    c: Distance(g131,g133) = 2.2
    c: Distance(g133,g132) = 1.5
    c: PointOnObject(g135,g132)
    c: Distance(g131,g135) = 1.1
    c: Coincident(g135,g116)
    c: Perpendicular(g116,g132)
    c: Coincident(g137,g136)
    c: Coincident(g138,g136)
    c: Coincident(g139,g138)
    c: Coincident(g139,g137)
    c: Parallel(g137,g138)
    c: Parallel(g136,g139)
    c: Perpendicular(g137,g136)
    c: Distance(g136,g138) = 2.2
    c: Distance(g138,g137) = 1.5
    c: PointOnObject(g140,g137)
    c: Distance(g136,g140) = 1.1
    c: Perpendicular(g141,g137)
    c: Coincident(g140,g141)
    c: Equal(g130,g141)
    c: Angle(g130,g141) = -0.261799
    c: Coincident(g142,g136)
    c: Coincident(g142,g136)
    c: Coincident(g143,g142)
    c: Coincident(g143,g138)
    c: Coincident(g144,g143)
    c: Coincident(g144,g137)
    c: Coincident(g145,g125)
    c: Coincident(g145,g144)
    c: Coincident(g146,g145)
    c: Coincident(g146,g125)
    c: Coincident(g147,g146)
    c: Coincident(g147,g127)
    c: Coincident(g148,g147)
    c: Coincident(g148,g126)
    c: Coincident(g149,g148)
    c: Coincident(g149,g119)
    c: Coincident(g150,g149)
    c: Coincident(g150,g119)
    c: Coincident(g151,g150)
    c: Coincident(g151,g121)
    c: Coincident(g152,g151)
    c: Coincident(g152,g120)
    c: Coincident(g153,g152)
    c: Coincident(g153,g131)
    c: Coincident(g154,g153)
    c: Coincident(g154,g131)
    c: Coincident(g155,g154)
    c: Coincident(g155,g133)
    c: Coincident(g156,g155)
    c: Coincident(g156,g132)
    c: Coincident(g157,g156)
    c: Coincident(g157,g117)
    c: Coincident(g159,g158)
    c: Coincident(g160,g158)
    c: Coincident(g161,g160)
    c: Coincident(g161,g159)
    c: Parallel(g159,g160)
    c: Parallel(g158,g161)
    c: Perpendicular(g159,g158)
    c: Distance(g158,g160) = 2.2
    c: Distance(g160,g159) = 1.5
    c: PointOnObject(g162,g159)
    c: Distance(g158,g162) = 1.1
    c: Perpendicular(g163,g159)
    c: Coincident(g162,g163)
    c: Coincident(g164,g159)
    c: Equal(g163,g141)
    c: Angle(g141,g163) = -0.261799
    c: Coincident(g166,g165)
    c: Coincident(g167,g165)
    c: Coincident(g168,g167)
    c: Coincident(g168,g166)
    c: Parallel(g166,g167)
    c: Parallel(g165,g168)
    c: Perpendicular(g166,g165)
    c: Distance(g165,g167) = 2.2
    c: Distance(g167,g166) = 1.5
    c: PointOnObject(g169,g166)
    c: Distance(g165,g169) = 1.1
    c: Perpendicular(g170,g166)
    c: Coincident(g169,g170)
    c: Coincident(g171,g166)
    c: Equal(g170,g163)
    c: Angle(g163,g170) = -0.261799
    c: Coincident(g172,g142)
    c: Coincident(g172,g164)
    c: Coincident(g173,g171)
    c: Coincident(g174,g157)
    c: Coincident(g96,g174)
    c: Coincident(g176,g175)
    c: Coincident(g177,g175)
    c: Parallel(g176,g177)
    c: Perpendicular(g176,g175)
    c: Distance(g175,g177) = 2.2
    c: Distance(g177,g176) = 1.5
    c: PointOnObject(g178,g176)
    c: Distance(g175,g178) = 1.1
    c: Coincident(g180,g179)
    c: Coincident(g181,g179)
    c: Coincident(g182,g181)
    c: Coincident(g182,g180)
    c: Parallel(g180,g181)
    c: Parallel(g179,g182)
    c: Perpendicular(g180,g179)
    c: Distance(g179,g181) = 2.2
    c: Distance(g181,g180) = 1.5
    c: PointOnObject(g183,g180)
    c: Distance(g179,g183) = 1.1
    c: Coincident(g185,g184)
    c: Coincident(g186,g184)
    c: Coincident(g187,g186)
    c: Coincident(g187,g185)
    c: Parallel(g185,g186)
    c: Parallel(g184,g187)
    c: Perpendicular(g185,g184)
    c: Distance(g184,g186) = 2.2
    c: Distance(g186,g185) = 1.5
    c: PointOnObject(g188,g185)
    c: Distance(g184,g188) = 1.1
    c: Coincident(g190,g189)
    c: Coincident(g191,g189)
    c: Coincident(g192,g191)
    c: Coincident(g192,g190)
    c: Parallel(g190,g191)
    c: Parallel(g189,g192)
    c: Perpendicular(g190,g189)
    c: Distance(g189,g191) = 2.2
    c: Distance(g191,g190) = 1.5
    c: PointOnObject(g193,g190)
    c: Distance(g189,g193) = 1.1
    c: Coincident(g195,g194)
    c: Coincident(g196,g194)
    c: Coincident(g197,g196)
    c: Coincident(g197,g195)
    c: Parallel(g195,g196)
    c: Parallel(g194,g197)
    c: Perpendicular(g195,g194)
    c: Distance(g194,g196) = 2.2
    c: Distance(g196,g195) = 1.5
    c: PointOnObject(g198,g195)
    c: Distance(g194,g198) = 1.1
    c: Coincident(g200,g199)
    c: Coincident(g201,g199)
    c: Coincident(g202,g201)
    c: Coincident(g202,g200)
    c: Parallel(g200,g201)
    c: Parallel(g199,g202)
    c: Perpendicular(g200,g199)
    c: Distance(g199,g201) = 2.2
    c: Distance(g201,g200) = 1.5
    c: PointOnObject(g203,g200)
    c: Distance(g199,g203) = 1.1
    c: Coincident(g205,g204)
    c: Coincident(g206,g204)
    c: Coincident(g207,g206)
    c: Coincident(g207,g205)
    c: Parallel(g205,g206)
    c: Parallel(g204,g207)
    c: Perpendicular(g205,g204)
    c: Distance(g204,g206) = 2.2
    c: Distance(g206,g205) = 1.5
    c: PointOnObject(g208,g205)
    c: Distance(g204,g208) = 1.1
    c: Coincident(g210,g209)
    c: Coincident(g211,g209)
    c: Coincident(g212,g211)
    c: Coincident(g212,g210)
    c: Parallel(g210,g211)
    c: Parallel(g209,g212)
    c: Perpendicular(g210,g209)
    c: Distance(g209,g211) = 2.2
    c: Distance(g211,g210) = 1.5
    c: PointOnObject(g213,g210)
    c: Distance(g209,g213) = 1.1
    c: Coincident(g215,g214)
    c: Coincident(g216,g214)
    c: Coincident(g217,g216)
    c: Coincident(g217,g215)
    c: Parallel(g215,g216)
    c: Parallel(g214,g217)
    c: Perpendicular(g215,g214)
    c: Distance(g214,g216) = 2.2
    c: Distance(g216,g215) = 1.5
    c: PointOnObject(g218,g215)
    c: Distance(g214,g218) = 1.1
    c: Coincident(g221,g220)
    c: Coincident(g222,g220)
    c: Coincident(g223,g222)
    c: Coincident(g223,g221)
    c: Parallel(g221,g222)
    c: Parallel(g220,g223)
    c: Perpendicular(g221,g220)
    c: Distance(g220,g222) = 2.2
    c: Distance(g222,g221) = 1.5
    c: PointOnObject(g224,g221)
    c: Distance(g220,g224) = 1.1
    c: Coincident(g225,g220)
    c: Coincident(g225,g220)
    c: Coincident(g226,g225)
    c: Coincident(g226,g222)
    c: Coincident(g227,g226)
    c: Coincident(g227,g221)
    c: Coincident(g228,g189)
    c: Coincident(g228,g227)
    c: Coincident(g229,g228)
    c: Coincident(g229,g189)
    c: Coincident(g230,g229)
    c: Coincident(g230,g191)
    c: Coincident(g231,g230)
    c: Coincident(g231,g190)
    c: Coincident(g232,g231)
    c: Coincident(g232,g184)
    c: Coincident(g233,g232)
    c: Coincident(g233,g184)
    c: Coincident(g234,g233)
    c: Coincident(g234,g186)
    c: Coincident(g235,g234)
    c: Coincident(g235,g185)
    c: Coincident(g236,g235)
    c: Coincident(g236,g194)
    c: Coincident(g237,g236)
    c: Coincident(g237,g194)
    c: Coincident(g238,g237)
    c: Coincident(g238,g196)
    c: Coincident(g239,g238)
    c: Coincident(g239,g195)
    c: Coincident(g240,g239)
    c: Coincident(g240,g175)
    c: Coincident(g241,g240)
    c: PointOnObject(g241,g177)
    c: Coincident(g242,g241)
    c: Coincident(g242,g177)
    c: Coincident(g244,g243)
    c: Coincident(g245,g243)
    c: Coincident(g246,g245)
    c: Coincident(g246,g244)
    c: Parallel(g244,g245)
    c: Parallel(g243,g246)
    c: Perpendicular(g244,g243)
    c: Distance(g243,g245) = 2.2
    c: Distance(g245,g244) = 1.5
    c: PointOnObject(g247,g244)
    c: Distance(g243,g247) = 1.1
    c: Coincident(g248,g243)
    c: Coincident(g248,g243)
    c: Coincident(g249,g248)
    c: Coincident(g249,g245)
    c: Coincident(g250,g249)
    c: Coincident(g250,g244)
    c: Coincident(g253,g225)
    c: Coincident(g253,g250)
    c: Coincident(g254,g248)
    c: Coincident(g254,g252)
    c: Distance(g255,g256) = 1.1
    c: Coincident(g258,g257)
    c: Coincident(g259,g257)
    c: Coincident(g260,g259)
    c: Coincident(g260,g258)
    c: Parallel(g258,g259)
    c: Parallel(g257,g260)
    c: Perpendicular(g258,g257)
    c: Distance(g257,g259) = 2.2
    c: Distance(g259,g258) = 1.5
    c: PointOnObject(g261,g258)
    c: Distance(g257,g261) = 1.1
    c: Coincident(g263,g262)
    c: Coincident(g264,g262)
    c: Coincident(g265,g264)
    c: Coincident(g265,g263)
    c: Parallel(g263,g264)
    c: Parallel(g262,g265)
    c: Perpendicular(g263,g262)
    c: Distance(g262,g264) = 2.2
    c: Distance(g264,g263) = 1.5
    c: PointOnObject(g266,g263)
    c: Distance(g262,g266) = 1.1
    c: Coincident(g268,g267)
    c: Coincident(g269,g267)
    c: Coincident(g270,g269)
    c: Coincident(g270,g268)
    c: Parallel(g268,g269)
    c: Parallel(g267,g270)
    c: Perpendicular(g268,g267)
    c: Distance(g267,g269) = 2.2
    c: Distance(g269,g268) = 1.5
    c: PointOnObject(g271,g268)
    c: Distance(g267,g271) = 1.1
    c: Coincident(g273,g272)
    c: Coincident(g274,g272)
    c: Coincident(g275,g274)
    c: Coincident(g275,g273)
    c: Parallel(g273,g274)
    c: Parallel(g272,g275)
    c: Perpendicular(g273,g272)
    c: Distance(g272,g274) = 2.2
    c: Distance(g274,g273) = 1.5
    c: PointOnObject(g276,g273)
    c: Distance(g272,g276) = 1.1
    c: Coincident(g277,g272)
    c: Coincident(g277,g272)
    c: Coincident(g278,g277)
    c: Coincident(g278,g274)
    c: Coincident(g279,g278)
    c: Coincident(g279,g273)
    c: Coincident(g280,g262)
    c: Coincident(g280,g279)
    c: Coincident(g281,g280)
    c: Coincident(g281,g262)
    c: Coincident(g282,g281)
    c: Coincident(g282,g264)
    c: Coincident(g283,g282)
    c: Coincident(g283,g263)
    c: Coincident(g284,g283)
    c: Coincident(g284,g257)
    c: Coincident(g285,g284)
    c: Coincident(g285,g257)
    c: Coincident(g286,g285)
    c: Coincident(g286,g259)
    c: Coincident(g287,g286)
    c: Coincident(g287,g258)
    c: Coincident(g288,g287)
    c: Coincident(g288,g267)
    c: Coincident(g289,g288)
    c: Coincident(g289,g267)
    c: Coincident(g290,g289)
    c: Coincident(g290,g269)
    c: Coincident(g291,g290)
    c: Coincident(g291,g268)
    c: Coincident(g292,g291)
    c: Coincident(g292,g255)
    c: Coincident(g294,g293)
    c: Coincident(g295,g293)
    c: Coincident(g296,g295)
    c: Coincident(g296,g294)
    c: Parallel(g294,g295)
    c: Parallel(g293,g296)
    c: Perpendicular(g294,g293)
    c: Distance(g293,g295) = 2.2
    c: Distance(g295,g294) = 1.5
    c: PointOnObject(g297,g294)
    c: Distance(g293,g297) = 1.1
    c: Coincident(g298,g293)
    c: Coincident(g298,g293)
    c: Coincident(g299,g298)
    c: Coincident(g299,g295)
    c: Coincident(g300,g299)
    c: Coincident(g300,g294)
    c: Coincident(g302,g277)
    c: Coincident(g302,g300)
    c: Coincident(g303,g298)
    c: Coincident(g304,g292)
    c: Coincident(g242,g304)
    c: Coincident(g305,g-1)
    c: Diameter(g305) = 30
    c: Coincident(g306,g173)
    c: Coincident(g307,g164)
    c: Coincident(g307,g306)
    c: Coincident(g308,g171)
    c: Coincident(g309,g308)
    c: Coincident(g309,g303)
    c: Coincident(g308,g58)
FEATURE [PartDesign::Pad] Pad
  Direction = (1,1,1)
  Length = 3
  Length2 = 100
  Profile = -> Sketch
  Type = 0
FEATURE [PartDesign::Body] Body
  Group = -> [Sketch,Pad]
  Origin = -> Origin
  Tip = -> Pad
